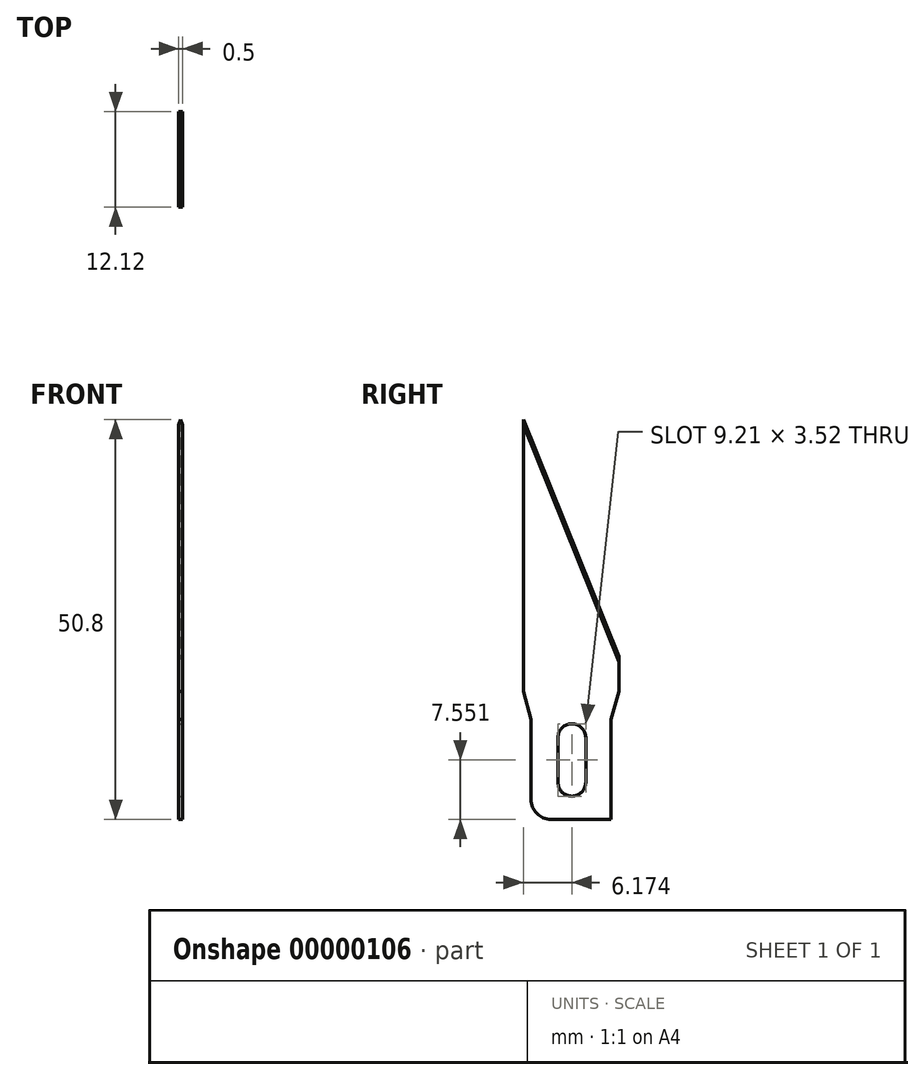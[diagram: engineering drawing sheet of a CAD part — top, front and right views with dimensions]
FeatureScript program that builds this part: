
annotation { "Feature Type Name" : "Feature", "Feature Type Description" : "" }
export const myFeature = defineFeature(function(context is Context, id is Id, definition is map)
    precondition{}
    {
        {
            var Q0;
            Q0=qCreatedBy(makeId("Right.planeOp"),FACE);
            var sketch = newSketch(context, id + "F0", { "sketchPlane" : qUnion([Q0])});
            skLineSegment(sketch, "E0", {"start": v(0, 0) * mm, "end": v(0, 12.7) * mm});
            skLineSegment(sketch, "E1", {"start": v(0.98, 20.7) * mm, "end": v(-11.14, 50.8) * mm});
            skLineSegment(sketch, "E2", {"start": v(-11.14, 50.8) * mm, "end": v(-11.14, 16.23) * mm});
            skLineSegment(sketch, "E3", {"start": v(-11.14, 16.23) * mm, "end": v(-10.16, 12.7) * mm});
            skLineSegment(sketch, "E4", {"start": v(-10.16, 12.7) * mm, "end": v(-10.16, 0) * mm});
            skLineSegment(sketch, "E5", {"start": v(-10.16, 0) * mm, "end": v(0, 0) * mm});
            skLineSegment(sketch, "E6", {"start": v(-5.08, 0) * mm, "end": v(-5.08, 16.23) * mm, "construction": true});
            skLineSegment(sketch, "E7.0.MirrorCS", {"start": v(0.98, 20.7) * mm, "end": v(0.98, 16.23) * mm});
            skLineSegment(sketch, "E8.0.MirrorCS", {"start": v(0.98, 16.23) * mm, "end": v(0, 12.7) * mm});
            skLineSegment(sketch, "E9", {"start": v(-11.14, 16.23) * mm, "end": v(0.98, 16.23) * mm, "construction": true});
            skLineSegment(sketch, "E10", {"start": v(-10.16, 12.7) * mm, "end": v(0, 12.7) * mm, "construction": true});
            skSolve(sketch);
        }
        {
            var Q0;
            Q0=makeQuery(id+"F0.imprint","IMPRINT",FACE,{"disambiguationData":[TD([[makeQuery(id+"F0.imprint","IMPRINT",EDGE,{"derivedFrom":sQuery(id+"F0.wireOp",EDGE,"E0")}),1.0]])]});
            extrude(context, id + "F1", {"entities" : qUnion([Q0]), "endBound" : BoundingType.SYMMETRIC, "depth" : 0.5 * mm});
        }
        {
            var Q0;
            Q0=makeQuery(id+"F1.opExtrude","CAP_EDGE",EDGE,{"disambiguationData":[OSD([sQuery(id+"F0.wireOp",EDGE,"E1")])],"isStart":false});
            var Q1;
            Q1=makeQuery(id+"F1.opExtrude","CAP_EDGE",EDGE,{"disambiguationData":[OSD([sQuery(id+"F0.wireOp",EDGE,"E1")])],"isStart":true});
            chamfer(context, id + "F2", {"entities" : qUnion([Q0, Q1]), "width" : 0.25 * mm, "tangentPropagation" : true});
        }
        {
            var Q0;
            Q0=makeQuery(id+"F1.opExtrude","SWEPT_EDGE",EDGE,{"disambiguationData":[OSD([sQuery(id+"F0.wireOp",EDGE,"E4"),sQuery(id+"F0.wireOp",EDGE,"E5")])]});
            fillet(context, id + "F3", {"entities" : qUnion([Q0]), "radius" : 2.54 * mm, "tangentPropagation" : true, "allowEdgeOverflow" : false});
        }
        {
            var Q0;
            Q0=makeQuery(id+"F1.opExtrude","CAP_FACE",FACE,{"disambiguationData":[OSD([sQuery(id+"F0.wireOp",EDGE,"E0"),sQuery(id+"F0.wireOp",EDGE,"E1"),sQuery(id+"F0.wireOp",EDGE,"E2"),sQuery(id+"F0.wireOp",EDGE,"E3"),sQuery(id+"F0.wireOp",EDGE,"E4"),sQuery(id+"F0.wireOp",EDGE,"E5"),sQuery(id+"F0.wireOp",EDGE,"E7.0.MirrorCS"),sQuery(id+"F0.wireOp",EDGE,"E8.0.MirrorCS")])],"isStart":false});
            var sketch = newSketch(context, id + "F4", { "sketchPlane" : qUnion([Q0])});
            skCircle(sketch, "E11", {"center": v(-4.97, 4.7) * mm, "radius": 1.76 * mm});
            skCircle(sketch, "E12", {"center": v(-4.97, 10.4) * mm, "radius": 1.76 * mm});
            skLineSegment(sketch, "E13", {"start": v(-6.73, 10.4) * mm, "end": v(-6.73, 4.7) * mm});
            skLineSegment(sketch, "E14", {"start": v(-3.2, 10.4) * mm, "end": v(-3.2, 4.7) * mm});
            skSolve(sketch);
        }
        {
            var Q0;
            {var subQ0=sQuery(id+"F4.wireOp",EDGE,"E11");var subQ3=sQuery(id+"F4.wireOp",EDGE,"E13");var subQ4=makeQuery(id+"F4.imprint","INTERSECT",VERTEX,{"derivedFrom":[subQ0,subQ3]});var subQ5=makeQuery(id+"F4.imprint","IMPRINT",EDGE,{"disambiguationData":[TD([[subQ4,1.0]])],"derivedFrom":subQ0});var subQ6=sQuery(id+"F4.wireOp",EDGE,"E12");var subQ8=makeQuery(id+"F4.imprint","INTERSECT",VERTEX,{"derivedFrom":[subQ6,subQ3]});Q0=qUnion([makeQuery(id+"F4.imprint","IMPRINT",FACE,{"disambiguationData":[TD([[subQ5,1.0]])]}),makeQuery(id+"F4.imprint","IMPRINT",FACE,{"disambiguationData":[TD([[makeQuery(id+"F4.imprint","IMPRINT",EDGE,{"disambiguationData":[TD([[subQ8,1.0]])],"derivedFrom":subQ6}),1.0]])]}),makeQuery(id+"F4.imprint","IMPRINT",FACE,{"disambiguationData":[TD([[makeQuery(id+"F4.imprint","IMPRINT",EDGE,{"derivedFrom":subQ3}),1.0]])]})]);}
            extrude(context, id + "F5", {"entities" : qUnion([Q0]), "operationType" : NewBodyOperationType.REMOVE, "endBound" : BoundingType.THROUGH_ALL, "oppositeDirection" : true, "depth" : 25.4 * mm});
        }
    });
